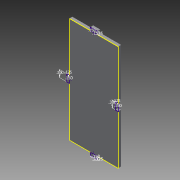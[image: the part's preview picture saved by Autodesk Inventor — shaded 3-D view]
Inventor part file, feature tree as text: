
AUTODESK INVENTOR PART (.ipt)
format: ipt  version: 2015 (Build 190159000, 159)  size: 107,520 bytes
history: native  units: in
note: dims shown in document units (in); Inventor stores cm internally (conversion verified against a paired STEP export)
features: extrude x3, sketch x2
ambient origin geometry x8: Origin, YZ Plane, XZ Plane, XY Plane, X Axis, Y Axis, Z Axis, Center Point
bodies: Solid1 (feature_tree)
feature tree (5):
  extrude  "Extrusion1"  Depth=2.084in
  sketch  "Sketch2"  dims[d2=0.125in d3=0.0in d4=0.15in d5=0.3in d6=0.125in d7=0.15in d8=0.3in d9=0.125in d10=0.15in d11=0.15in d12=0.125in d13=0.3in d14=0.15in d15=0.125in d16=0.125in d17=0.0in d18=0.125in d19=0.0in]
  extrude  "Extrusion2"  Depth=0.125in
  extrude  "Extrusion3"  Depth=0.3in
  sketch  "Sketch1"  dims[d0=4.5in d1=2.084in]
